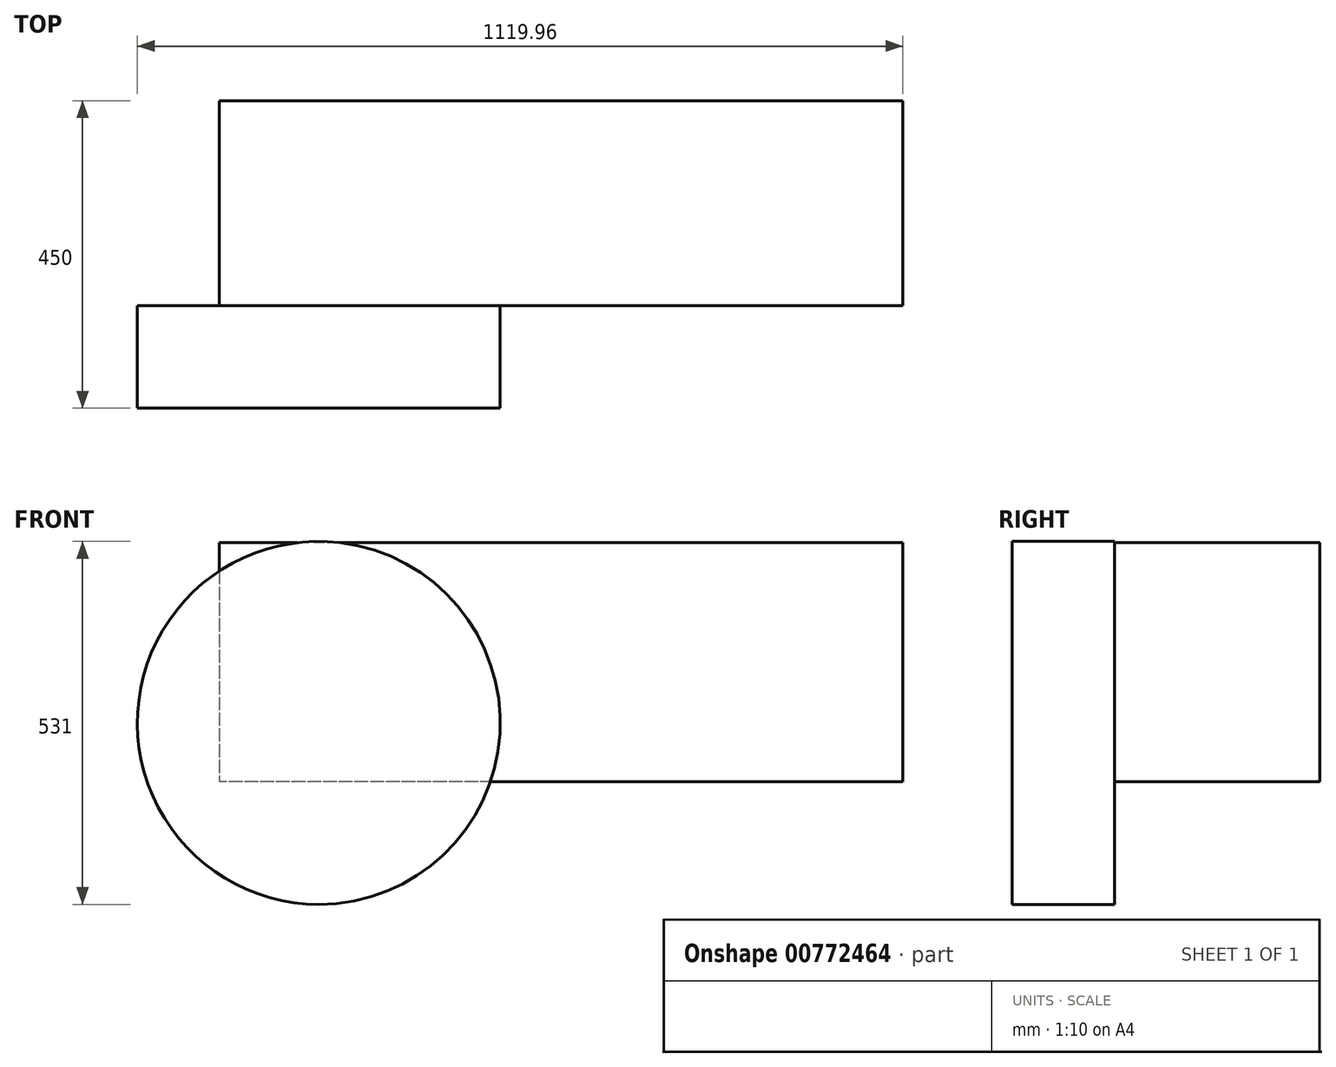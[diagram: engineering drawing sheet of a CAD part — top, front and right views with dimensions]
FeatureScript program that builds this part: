
annotation { "Feature Type Name" : "Feature", "Feature Type Description" : "" }
export const myFeature = defineFeature(function(context is Context, id is Id, definition is map)
    precondition{}
    {
        {
            var Q0;
            Q0=qCreatedBy(makeId("Top.planeOp"),FACE);
            var sketch = newSketch(context, id + "F0", { "sketchPlane" : qUnion([Q0])});
            skLineSegment(sketch, "E0.bottom", {"start": v(500, 150) * mm, "end": v(-500, 150) * mm});
            skLineSegment(sketch, "E0.top", {"start": v(500, -150) * mm, "end": v(-500, -150) * mm});
            skLineSegment(sketch, "E0.left", {"start": v(500, 150) * mm, "end": v(500, -150) * mm});
            skLineSegment(sketch, "E0.right", {"start": v(-500, 150) * mm, "end": v(-500, -150) * mm});
            skPoint(sketch, "E0.middle", {"position": v(0, 0) * mm});
            skSolve(sketch);
        }
        {
            var Q0;
            Q0 = qSketchRegion(id + "F0", true);
            extrude(context, id + "F1", {"entities" : qUnion([Q0]), "depth" : 350 * mm, "offsetDistance" : 25 * mm});
        }
        {
            var Q0;
            Q0=makeQuery(id+"F1.opExtrude","SWEPT_FACE",FACE,{"disambiguationData":[OSD([sQuery(id+"F0.wireOp",EDGE,"E0.top")])]});
            var sketch = newSketch(context, id + "F2", { "sketchPlane" : qUnion([Q0])});
            skCircle(sketch, "E1", {"center": v(-354.46, 86.3) * mm, "radius": 190.5 * mm});
            skCircle(sketch, "E2", {"center": v(-354.46, 86.3) * mm, "radius": 265.5 * mm});
            skSolve(sketch);
        }
        {
            var Q0;
            Q0 = qSketchRegion(id + "F2", true);
            var Q1;
            {var subQ0=sQuery(id+"F2.wireOp",EDGE,"E1");var subQ1=sQuery(id+"F0.wireOp",EDGE,"E0.top");var subQ4=makeQuery(id+"F1.opExtrude","CAP_EDGE",EDGE,{"disambiguationData":[OSD([subQ1])],"isStart":true});var subQ5=makeQuery(id+"F2.imprint","INTERSECT",VERTEX,{"derivedFrom":[subQ4,subQ0]});Q1=makeQuery(id+"F2.imprint","IMPRINT",FACE,{"disambiguationData":[TD([[makeQuery(id+"F2.imprint","IMPRINT",EDGE,{"disambiguationData":[TD([[subQ5,-1.0]])],"derivedFrom":subQ0}),1.0]])]});}
            var Q2;
            {var subQ0=sQuery(id+"F2.wireOp",EDGE,"E1");var subQ1=sQuery(id+"F0.wireOp",EDGE,"E0.top");var subQ4=makeQuery(id+"F1.opExtrude","CAP_EDGE",EDGE,{"disambiguationData":[OSD([subQ1])],"isStart":true});var subQ5=makeQuery(id+"F2.imprint","INTERSECT",VERTEX,{"derivedFrom":[subQ4,subQ0]});Q2=makeQuery(id+"F2.imprint","IMPRINT",FACE,{"disambiguationData":[TD([[makeQuery(id+"F2.imprint","IMPRINT",EDGE,{"disambiguationData":[TD([[subQ5,1.0]])],"derivedFrom":subQ0}),1.0]])]});}
            extrude(context, id + "F3", {"entities" : qUnion([Q0, Q1, Q2]), "operationType" : NewBodyOperationType.ADD, "depth" : 150 * mm, "offsetDistance" : 25 * mm});
        }
    });
